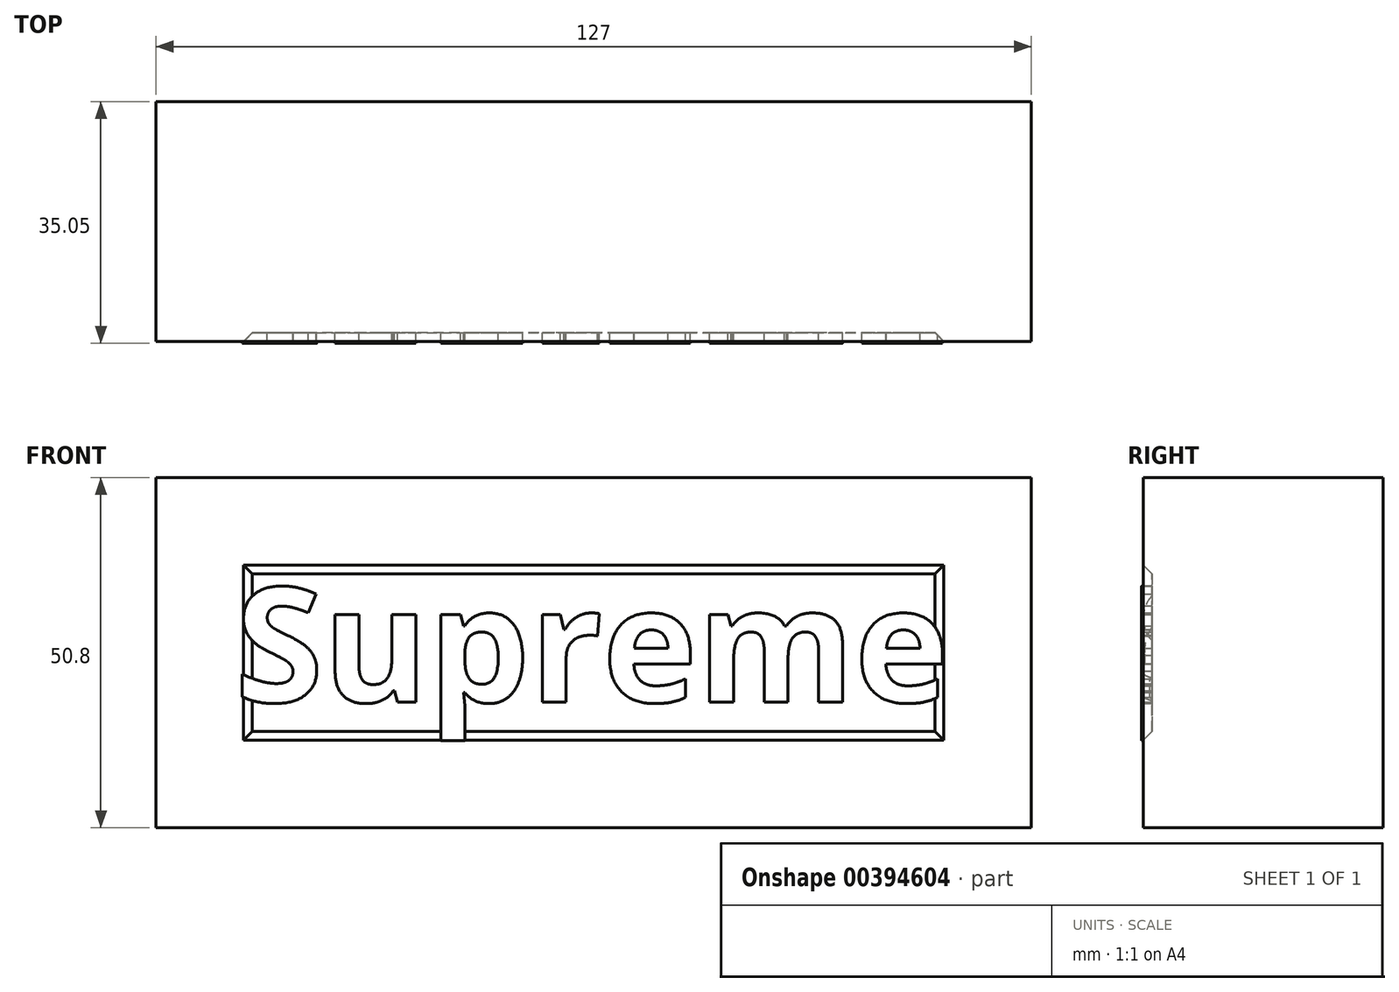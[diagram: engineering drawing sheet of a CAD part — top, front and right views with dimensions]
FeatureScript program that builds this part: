
annotation { "Feature Type Name" : "Feature", "Feature Type Description" : "" }
export const myFeature = defineFeature(function(context is Context, id is Id, definition is map)
    precondition{}
    {
        {
            var Q0;
            Q0=qCreatedBy(makeId("Front.planeOp"),FACE);
            var sketch = newSketch(context, id + "F0", { "sketchPlane" : qUnion([Q0])});
            skLineSegment(sketch, "E0.bottom", {"start": v(0, 0) * mm, "end": v(-127, 0) * mm});
            skLineSegment(sketch, "E0.top", {"start": v(0, -50.8) * mm, "end": v(-127, -50.8) * mm});
            skLineSegment(sketch, "E0.left", {"start": v(0, 0) * mm, "end": v(0, -50.8) * mm});
            skLineSegment(sketch, "E0.right", {"start": v(-127, 0) * mm, "end": v(-127, -50.8) * mm});
            skSolve(sketch);
        }
        {
            var Q0;
            Q0=makeQuery(id+"F0.imprint","IMPRINT",FACE,{"disambiguationData":[TD([[makeQuery(id+"F0.imprint","IMPRINT",EDGE,{"derivedFrom":sQuery(id+"F0.wireOp",EDGE,"E0.bottom")}),1.0]])]});
            extrude(context, id + "F1", {"entities" : qUnion([Q0]), "depth" : 34.8 * mm});
        }
        {
            var Q0;
            Q0=makeQuery(id+"F1.opExtrude","CAP_FACE",FACE,{"disambiguationData":[OSD([sQuery(id+"F0.wireOp",EDGE,"E0.bottom"),sQuery(id+"F0.wireOp",EDGE,"E0.top"),sQuery(id+"F0.wireOp",EDGE,"E0.left"),sQuery(id+"F0.wireOp",EDGE,"E0.right")])],"isStart":false});
            var sketch = newSketch(context, id + "F2", { "sketchPlane" : qUnion([Q0])});
            skLineSegment(sketch, "E1.0", {"start": v(-115.57, -39.37) * mm, "end": v(-11.43, -39.37) * mm});
            skLineSegment(sketch, "E1.1", {"start": v(-115.57, -11.43) * mm, "end": v(-115.57, -39.37) * mm});
            skLineSegment(sketch, "E1.2", {"start": v(-11.43, -11.43) * mm, "end": v(-115.57, -11.43) * mm});
            skLineSegment(sketch, "E1.3", {"start": v(-11.43, -39.37) * mm, "end": v(-11.43, -11.43) * mm});
            skSolve(sketch);
        }
        {
            var Q0;
            Q0=makeQuery(id+"F2.imprint","IMPRINT",FACE,{"disambiguationData":[TD([[makeQuery(id+"F2.imprint","IMPRINT",EDGE,{"derivedFrom":sQuery(id+"F2.wireOp",EDGE,"E1.0")}),1.0]])]});
            var Q1;
            Q1 = qSketchRegion(id + "F4", true);
            extrude(context, id + "F3", {"entities" : qUnion([Q0, Q1]), "operationType" : NewBodyOperationType.REMOVE, "oppositeDirection" : true, "depth" : 1.27 * mm});
        }
        {
            var Q0;
            Q0=makeQuery(id+"F3.boolean.opBoolean","COPY",FACE,{"derivedFrom":makeQuery(id+"F3.opExtrude","CAP_FACE",FACE,{"disambiguationData":[OSD([sQuery(id+"F2.wireOp",EDGE,"E1.0"),sQuery(id+"F2.wireOp",EDGE,"E1.1"),sQuery(id+"F2.wireOp",EDGE,"E1.2"),sQuery(id+"F2.wireOp",EDGE,"E1.3")])],"isStart":false})});
            var sketch = newSketch(context, id + "F4", { "sketchPlane" : qUnion([Q0])});
            skText(sketch, "E2", { "text": "Supreme", "fontName": "OpenSans-Bold.ttf"});
            const initialGuessF4  = {"E2": [-0.11557, -0.03256, 1, 0, 0.01674]};
            skSetInitialGuess(sketch, initialGuessF4);
            skSolve(sketch);
        }
        {
            var Q0;
            Q0 = qSketchRegion(id + "F4", true);
            extrude(context, id + "F5", {"entities" : qUnion([Q0]), "operationType" : NewBodyOperationType.ADD, "depth" : 1.52 * mm});
        }
        {
            var Q0;
            Q0=makeQuery(id+"F3.boolean.opBoolean","COPY",EDGE,{"derivedFrom":makeQuery(id+"F3.opExtrude","CAP_EDGE",EDGE,{"disambiguationData":[OSD([sQuery(id+"F2.wireOp",EDGE,"E1.2")])],"isStart":false})});
            var Q1;
            Q1=makeQuery(id+"F3.boolean.opBoolean","COPY",EDGE,{"derivedFrom":makeQuery(id+"F3.opExtrude","CAP_EDGE",EDGE,{"disambiguationData":[OSD([sQuery(id+"F2.wireOp",EDGE,"E1.0")])],"isStart":false})});
            chamfer(context, id + "F6", {"entities" : qUnion([Q0, Q1]), "width" : 2.54 * mm, "tangentPropagation" : true});
        }
        {
            var Q0;
            Q0=makeQuery(id+"F3.boolean.opBoolean","COPY",EDGE,{"derivedFrom":makeQuery(id+"F3.opExtrude","CAP_EDGE",EDGE,{"disambiguationData":[OSD([sQuery(id+"F2.wireOp",EDGE,"E1.3")])],"isStart":false})});
            var Q1;
            Q1=makeQuery(id+"F3.boolean.opBoolean","COPY",EDGE,{"derivedFrom":makeQuery(id+"F3.opExtrude","CAP_EDGE",EDGE,{"disambiguationData":[OSD([sQuery(id+"F2.wireOp",EDGE,"E1.1")])],"isStart":false})});
            chamfer(context, id + "F7", {"entities" : qUnion([Q0, Q1]), "width" : 2.54 * mm, "tangentPropagation" : true});
        }
    });
